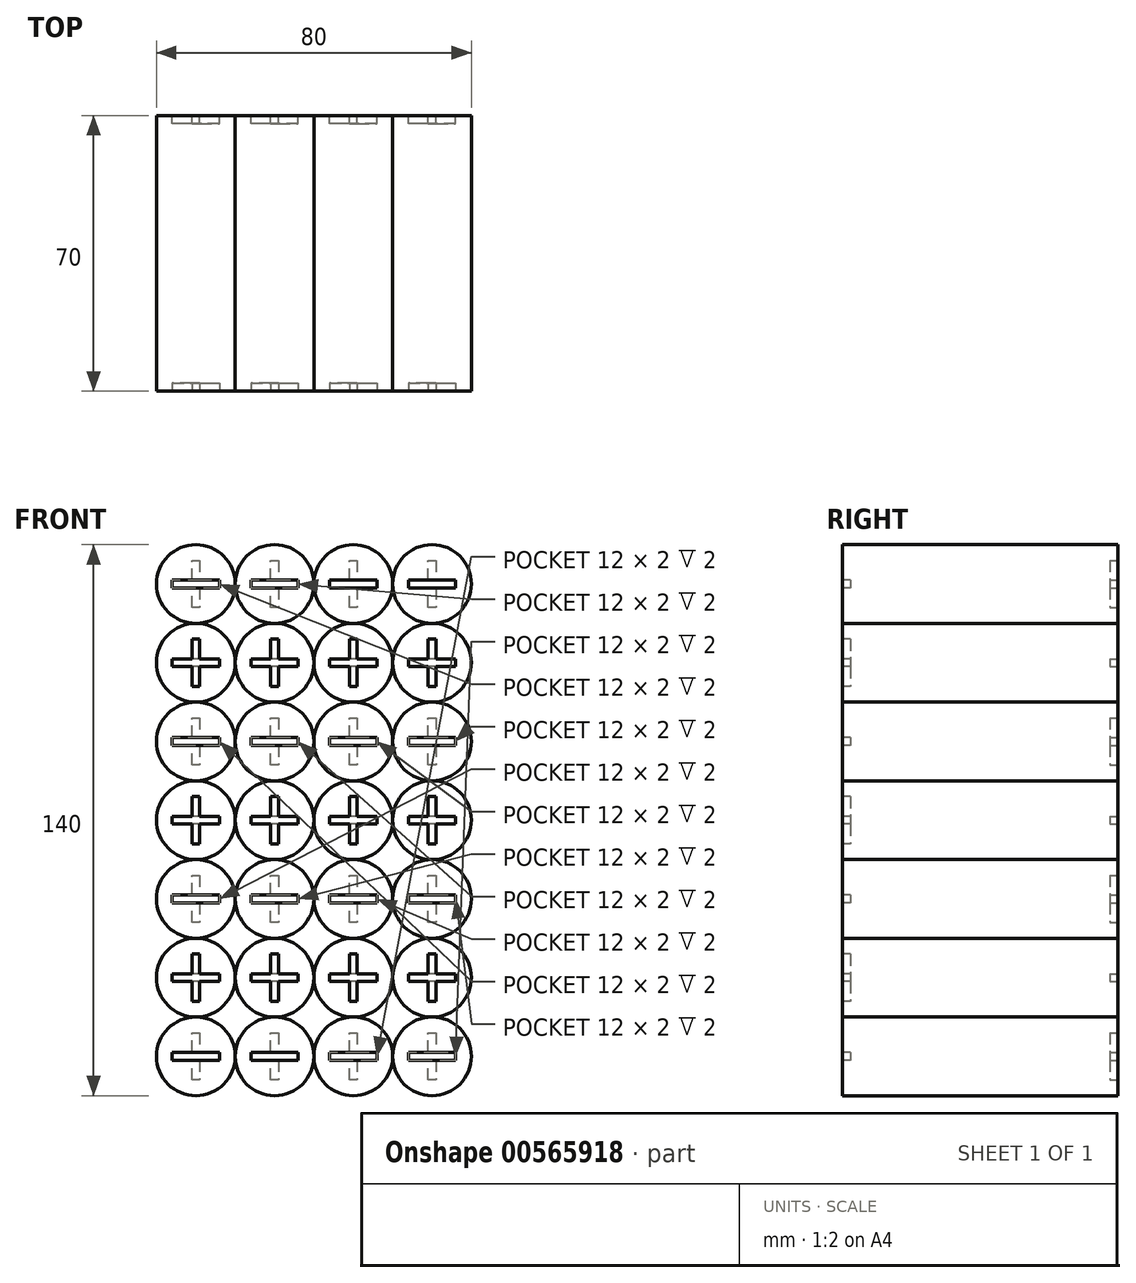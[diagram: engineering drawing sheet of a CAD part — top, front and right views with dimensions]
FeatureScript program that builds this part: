
annotation { "Feature Type Name" : "Feature", "Feature Type Description" : "" }
export const myFeature = defineFeature(function(context is Context, id is Id, definition is map)
    precondition{}
    {
        {
            var Q0;
            Q0=qCreatedBy(makeId("Front.planeOp"),FACE);
            var sketch = newSketch(context, id + "F0", { "sketchPlane" : qUnion([Q0])});
            skCircle(sketch, "E0", {"center": v(10, 10) * mm, "radius": 10 * mm});
            skCircle(sketch, "E1", {"center": v(30, 10) * mm, "radius": 10 * mm});
            skCircle(sketch, "E2", {"center": v(50, 10) * mm, "radius": 10 * mm});
            skCircle(sketch, "E3", {"center": v(70, 10) * mm, "radius": 10 * mm});
            skCircle(sketch, "E4", {"center": v(10, 30) * mm, "radius": 10 * mm});
            skCircle(sketch, "E5", {"center": v(30, 30) * mm, "radius": 10 * mm});
            skCircle(sketch, "E6", {"center": v(50, 30) * mm, "radius": 10 * mm});
            skCircle(sketch, "E7", {"center": v(70, 30) * mm, "radius": 10 * mm});
            skCircle(sketch, "E8", {"center": v(10, 50) * mm, "radius": 10 * mm});
            skCircle(sketch, "E9", {"center": v(30, 50) * mm, "radius": 10 * mm});
            skCircle(sketch, "E10", {"center": v(50, 50) * mm, "radius": 10 * mm});
            skCircle(sketch, "E11", {"center": v(70, 50) * mm, "radius": 10 * mm});
            skCircle(sketch, "E12", {"center": v(10, 70) * mm, "radius": 10 * mm});
            skCircle(sketch, "E13", {"center": v(30, 70) * mm, "radius": 10 * mm});
            skCircle(sketch, "E14", {"center": v(50, 70) * mm, "radius": 10 * mm});
            skCircle(sketch, "E15", {"center": v(70, 70) * mm, "radius": 10 * mm});
            skCircle(sketch, "E16", {"center": v(10, 90) * mm, "radius": 10 * mm});
            skCircle(sketch, "E17", {"center": v(30, 90) * mm, "radius": 10 * mm});
            skCircle(sketch, "E18", {"center": v(50, 90) * mm, "radius": 10 * mm});
            skCircle(sketch, "E19", {"center": v(70, 90) * mm, "radius": 10 * mm});
            skCircle(sketch, "E20", {"center": v(10, 110) * mm, "radius": 10 * mm});
            skCircle(sketch, "E21", {"center": v(30, 110) * mm, "radius": 10 * mm});
            skCircle(sketch, "E22", {"center": v(50, 110) * mm, "radius": 10 * mm});
            skCircle(sketch, "E23", {"center": v(70, 110) * mm, "radius": 10 * mm});
            skCircle(sketch, "E24", {"center": v(10, 130) * mm, "radius": 10 * mm});
            skCircle(sketch, "E25", {"center": v(30, 130) * mm, "radius": 10 * mm});
            skCircle(sketch, "E26", {"center": v(50, 130) * mm, "radius": 10 * mm});
            skCircle(sketch, "E27", {"center": v(70, 130) * mm, "radius": 10 * mm});
            skSolve(sketch);
        }
        {
            var Q0;
            Q0 = qSketchRegion(id + "F0", true);
            extrude(context, id + "F1", {"entities" : qUnion([Q0]), "depth" : 70 * mm, "offsetDistance" : 25 * mm});
        }
        {
            var Q0;
            Q0=makeQuery(id+"F1.opExtrude","CAP_FACE",FACE,{"disambiguationData":[OSD([sQuery(id+"F0.wireOp",EDGE,"E5")])],"isStart":true});
            var sketch = newSketch(context, id + "F2", { "sketchPlane" : qUnion([Q0])});
            skLineSegment(sketch, "E28", {"start": v(-71, 16) * mm, "end": v(-71, 11) * mm});
            skLineSegment(sketch, "E29", {"start": v(-71, 11) * mm, "end": v(-76, 11) * mm});
            skLineSegment(sketch, "E30", {"start": v(-76, 11) * mm, "end": v(-76, 9) * mm});
            skLineSegment(sketch, "E31", {"start": v(-76, 9) * mm, "end": v(-71, 9) * mm});
            skLineSegment(sketch, "E32", {"start": v(-71, 9) * mm, "end": v(-71, 4) * mm});
            skLineSegment(sketch, "E33", {"start": v(-71, 4) * mm, "end": v(-69, 4) * mm});
            skLineSegment(sketch, "E34", {"start": v(-69, 4) * mm, "end": v(-69, 9) * mm});
            skLineSegment(sketch, "E35", {"start": v(-69, 9) * mm, "end": v(-64, 9) * mm});
            skLineSegment(sketch, "E36", {"start": v(-64, 9) * mm, "end": v(-64, 11) * mm});
            skLineSegment(sketch, "E37", {"start": v(-64, 11) * mm, "end": v(-69, 11) * mm});
            skLineSegment(sketch, "E38", {"start": v(-69, 11) * mm, "end": v(-69, 16) * mm});
            skLineSegment(sketch, "E39", {"start": v(-69, 16) * mm, "end": v(-71, 16) * mm});
            skLineSegment(sketch, "E40", {"start": v(-11, 16) * mm, "end": v(-11, 11) * mm});
            skLineSegment(sketch, "E41", {"start": v(-11, 11) * mm, "end": v(-16, 11) * mm});
            skLineSegment(sketch, "E42", {"start": v(-16, 11) * mm, "end": v(-16, 9) * mm});
            skLineSegment(sketch, "E43", {"start": v(-16, 9) * mm, "end": v(-11, 9) * mm});
            skLineSegment(sketch, "E44", {"start": v(-11, 9) * mm, "end": v(-11, 4) * mm});
            skLineSegment(sketch, "E45", {"start": v(-11, 4) * mm, "end": v(-9, 4) * mm});
            skLineSegment(sketch, "E46", {"start": v(-9, 4) * mm, "end": v(-9, 9) * mm});
            skLineSegment(sketch, "E47", {"start": v(-9, 9) * mm, "end": v(-4, 9) * mm});
            skLineSegment(sketch, "E48", {"start": v(-4, 9) * mm, "end": v(-4, 11) * mm});
            skLineSegment(sketch, "E49", {"start": v(-4, 11) * mm, "end": v(-9, 11) * mm});
            skLineSegment(sketch, "E50", {"start": v(-9, 11) * mm, "end": v(-9, 16) * mm});
            skLineSegment(sketch, "E51", {"start": v(-9, 16) * mm, "end": v(-11, 16) * mm});
            skLineSegment(sketch, "E52", {"start": v(-31, 16) * mm, "end": v(-31, 11) * mm});
            skLineSegment(sketch, "E53", {"start": v(-31, 11) * mm, "end": v(-36, 11) * mm});
            skLineSegment(sketch, "E54", {"start": v(-36, 11) * mm, "end": v(-36, 9) * mm});
            skLineSegment(sketch, "E55", {"start": v(-36, 9) * mm, "end": v(-31, 9) * mm});
            skLineSegment(sketch, "E56", {"start": v(-31, 9) * mm, "end": v(-31, 4) * mm});
            skLineSegment(sketch, "E57", {"start": v(-31, 4) * mm, "end": v(-29, 4) * mm});
            skLineSegment(sketch, "E58", {"start": v(-29, 4) * mm, "end": v(-29, 9) * mm});
            skLineSegment(sketch, "E59", {"start": v(-29, 9) * mm, "end": v(-24, 9) * mm});
            skLineSegment(sketch, "E60", {"start": v(-24, 9) * mm, "end": v(-24, 11) * mm});
            skLineSegment(sketch, "E61", {"start": v(-24, 11) * mm, "end": v(-29, 11) * mm});
            skLineSegment(sketch, "E62", {"start": v(-29, 11) * mm, "end": v(-29, 16) * mm});
            skLineSegment(sketch, "E63", {"start": v(-29, 16) * mm, "end": v(-31, 16) * mm});
            skLineSegment(sketch, "E64", {"start": v(-51, 16) * mm, "end": v(-51, 11) * mm});
            skLineSegment(sketch, "E65", {"start": v(-51, 11) * mm, "end": v(-56, 11) * mm});
            skLineSegment(sketch, "E66", {"start": v(-56, 11) * mm, "end": v(-56, 9) * mm});
            skLineSegment(sketch, "E67", {"start": v(-56, 9) * mm, "end": v(-51, 9) * mm});
            skLineSegment(sketch, "E68", {"start": v(-51, 9) * mm, "end": v(-51, 4) * mm});
            skLineSegment(sketch, "E69", {"start": v(-51, 4) * mm, "end": v(-49, 4) * mm});
            skLineSegment(sketch, "E70", {"start": v(-49, 4) * mm, "end": v(-49, 9) * mm});
            skLineSegment(sketch, "E71", {"start": v(-49, 9) * mm, "end": v(-44, 9) * mm});
            skLineSegment(sketch, "E72", {"start": v(-44, 9) * mm, "end": v(-44, 11) * mm});
            skLineSegment(sketch, "E73", {"start": v(-44, 11) * mm, "end": v(-49, 11) * mm});
            skLineSegment(sketch, "E74", {"start": v(-49, 11) * mm, "end": v(-49, 16) * mm});
            skLineSegment(sketch, "E75", {"start": v(-49, 16) * mm, "end": v(-51, 16) * mm});
            skLineSegment(sketch, "E76", {"start": v(-71, 56) * mm, "end": v(-71, 51) * mm});
            skLineSegment(sketch, "E77", {"start": v(-71, 51) * mm, "end": v(-76, 51) * mm});
            skLineSegment(sketch, "E78", {"start": v(-76, 51) * mm, "end": v(-76, 49) * mm});
            skLineSegment(sketch, "E79", {"start": v(-76, 49) * mm, "end": v(-71, 49) * mm});
            skLineSegment(sketch, "E80", {"start": v(-71, 49) * mm, "end": v(-71, 44) * mm});
            skLineSegment(sketch, "E81", {"start": v(-71, 44) * mm, "end": v(-69, 44) * mm});
            skLineSegment(sketch, "E82", {"start": v(-69, 44) * mm, "end": v(-69, 49) * mm});
            skLineSegment(sketch, "E83", {"start": v(-69, 49) * mm, "end": v(-64, 49) * mm});
            skLineSegment(sketch, "E84", {"start": v(-64, 49) * mm, "end": v(-64, 51) * mm});
            skLineSegment(sketch, "E85", {"start": v(-64, 51) * mm, "end": v(-69, 51) * mm});
            skLineSegment(sketch, "E86", {"start": v(-69, 51) * mm, "end": v(-69, 56) * mm});
            skLineSegment(sketch, "E87", {"start": v(-69, 56) * mm, "end": v(-71, 56) * mm});
            skLineSegment(sketch, "E88", {"start": v(-11, 56) * mm, "end": v(-11, 51) * mm});
            skLineSegment(sketch, "E89", {"start": v(-11, 51) * mm, "end": v(-16, 51) * mm});
            skLineSegment(sketch, "E90", {"start": v(-16, 51) * mm, "end": v(-16, 49) * mm});
            skLineSegment(sketch, "E91", {"start": v(-16, 49) * mm, "end": v(-11, 49) * mm});
            skLineSegment(sketch, "E92", {"start": v(-11, 49) * mm, "end": v(-11, 44) * mm});
            skLineSegment(sketch, "E93", {"start": v(-11, 44) * mm, "end": v(-9, 44) * mm});
            skLineSegment(sketch, "E94", {"start": v(-9, 44) * mm, "end": v(-9, 49) * mm});
            skLineSegment(sketch, "E95", {"start": v(-9, 49) * mm, "end": v(-4, 49) * mm});
            skLineSegment(sketch, "E96", {"start": v(-4, 49) * mm, "end": v(-4, 51) * mm});
            skLineSegment(sketch, "E97", {"start": v(-4, 51) * mm, "end": v(-9, 51) * mm});
            skLineSegment(sketch, "E98", {"start": v(-9, 51) * mm, "end": v(-9, 56) * mm});
            skLineSegment(sketch, "E99", {"start": v(-9, 56) * mm, "end": v(-11, 56) * mm});
            skLineSegment(sketch, "E100", {"start": v(-31, 56) * mm, "end": v(-31, 51) * mm});
            skLineSegment(sketch, "E101", {"start": v(-31, 51) * mm, "end": v(-36, 51) * mm});
            skLineSegment(sketch, "E102", {"start": v(-36, 51) * mm, "end": v(-36, 49) * mm});
            skLineSegment(sketch, "E103", {"start": v(-36, 49) * mm, "end": v(-31, 49) * mm});
            skLineSegment(sketch, "E104", {"start": v(-31, 49) * mm, "end": v(-31, 44) * mm});
            skLineSegment(sketch, "E105", {"start": v(-31, 44) * mm, "end": v(-29, 44) * mm});
            skLineSegment(sketch, "E106", {"start": v(-29, 44) * mm, "end": v(-29, 49) * mm});
            skLineSegment(sketch, "E107", {"start": v(-29, 49) * mm, "end": v(-24, 49) * mm});
            skLineSegment(sketch, "E108", {"start": v(-24, 49) * mm, "end": v(-24, 51) * mm});
            skLineSegment(sketch, "E109", {"start": v(-24, 51) * mm, "end": v(-29, 51) * mm});
            skLineSegment(sketch, "E110", {"start": v(-29, 51) * mm, "end": v(-29, 56) * mm});
            skLineSegment(sketch, "E111", {"start": v(-29, 56) * mm, "end": v(-31, 56) * mm});
            skLineSegment(sketch, "E112", {"start": v(-51, 56) * mm, "end": v(-51, 51) * mm});
            skLineSegment(sketch, "E113", {"start": v(-51, 51) * mm, "end": v(-56, 51) * mm});
            skLineSegment(sketch, "E114", {"start": v(-56, 51) * mm, "end": v(-56, 49) * mm});
            skLineSegment(sketch, "E115", {"start": v(-56, 49) * mm, "end": v(-51, 49) * mm});
            skLineSegment(sketch, "E116", {"start": v(-51, 49) * mm, "end": v(-51, 44) * mm});
            skLineSegment(sketch, "E117", {"start": v(-51, 44) * mm, "end": v(-49, 44) * mm});
            skLineSegment(sketch, "E118", {"start": v(-49, 44) * mm, "end": v(-49, 49) * mm});
            skLineSegment(sketch, "E119", {"start": v(-49, 49) * mm, "end": v(-44, 49) * mm});
            skLineSegment(sketch, "E120", {"start": v(-44, 49) * mm, "end": v(-44, 51) * mm});
            skLineSegment(sketch, "E121", {"start": v(-44, 51) * mm, "end": v(-49, 51) * mm});
            skLineSegment(sketch, "E122", {"start": v(-49, 51) * mm, "end": v(-49, 56) * mm});
            skLineSegment(sketch, "E123", {"start": v(-49, 56) * mm, "end": v(-51, 56) * mm});
            skLineSegment(sketch, "E124", {"start": v(-71, 96) * mm, "end": v(-71, 91) * mm});
            skLineSegment(sketch, "E125", {"start": v(-71, 91) * mm, "end": v(-76, 91) * mm});
            skLineSegment(sketch, "E126", {"start": v(-76, 91) * mm, "end": v(-76, 89) * mm});
            skLineSegment(sketch, "E127", {"start": v(-76, 89) * mm, "end": v(-71, 89) * mm});
            skLineSegment(sketch, "E128", {"start": v(-71, 89) * mm, "end": v(-71, 84) * mm});
            skLineSegment(sketch, "E129", {"start": v(-71, 84) * mm, "end": v(-69, 84) * mm});
            skLineSegment(sketch, "E130", {"start": v(-69, 84) * mm, "end": v(-69, 89) * mm});
            skLineSegment(sketch, "E131", {"start": v(-69, 89) * mm, "end": v(-64, 89) * mm});
            skLineSegment(sketch, "E132", {"start": v(-64, 89) * mm, "end": v(-64, 91) * mm});
            skLineSegment(sketch, "E133", {"start": v(-64, 91) * mm, "end": v(-69, 91) * mm});
            skLineSegment(sketch, "E134", {"start": v(-69, 91) * mm, "end": v(-69, 96) * mm});
            skLineSegment(sketch, "E135", {"start": v(-69, 96) * mm, "end": v(-71, 96) * mm});
            skLineSegment(sketch, "E136", {"start": v(-11, 96) * mm, "end": v(-11, 91) * mm});
            skLineSegment(sketch, "E137", {"start": v(-11, 91) * mm, "end": v(-16, 91) * mm});
            skLineSegment(sketch, "E138", {"start": v(-16, 91) * mm, "end": v(-16, 89) * mm});
            skLineSegment(sketch, "E139", {"start": v(-16, 89) * mm, "end": v(-11, 89) * mm});
            skLineSegment(sketch, "E140", {"start": v(-11, 89) * mm, "end": v(-11, 84) * mm});
            skLineSegment(sketch, "E141", {"start": v(-11, 84) * mm, "end": v(-9, 84) * mm});
            skLineSegment(sketch, "E142", {"start": v(-9, 84) * mm, "end": v(-9, 89) * mm});
            skLineSegment(sketch, "E143", {"start": v(-9, 89) * mm, "end": v(-4, 89) * mm});
            skLineSegment(sketch, "E144", {"start": v(-4, 89) * mm, "end": v(-4, 91) * mm});
            skLineSegment(sketch, "E145", {"start": v(-4, 91) * mm, "end": v(-9, 91) * mm});
            skLineSegment(sketch, "E146", {"start": v(-9, 91) * mm, "end": v(-9, 96) * mm});
            skLineSegment(sketch, "E147", {"start": v(-9, 96) * mm, "end": v(-11, 96) * mm});
            skLineSegment(sketch, "E148", {"start": v(-31, 96) * mm, "end": v(-31, 91) * mm});
            skLineSegment(sketch, "E149", {"start": v(-31, 91) * mm, "end": v(-36, 91) * mm});
            skLineSegment(sketch, "E150", {"start": v(-36, 91) * mm, "end": v(-36, 89) * mm});
            skLineSegment(sketch, "E151", {"start": v(-36, 89) * mm, "end": v(-31, 89) * mm});
            skLineSegment(sketch, "E152", {"start": v(-31, 89) * mm, "end": v(-31, 84) * mm});
            skLineSegment(sketch, "E153", {"start": v(-31, 84) * mm, "end": v(-29, 84) * mm});
            skLineSegment(sketch, "E154", {"start": v(-29, 84) * mm, "end": v(-29, 89) * mm});
            skLineSegment(sketch, "E155", {"start": v(-29, 89) * mm, "end": v(-24, 89) * mm});
            skLineSegment(sketch, "E156", {"start": v(-24, 89) * mm, "end": v(-24, 91) * mm});
            skLineSegment(sketch, "E157", {"start": v(-24, 91) * mm, "end": v(-29, 91) * mm});
            skLineSegment(sketch, "E158", {"start": v(-29, 91) * mm, "end": v(-29, 96) * mm});
            skLineSegment(sketch, "E159", {"start": v(-29, 96) * mm, "end": v(-31, 96) * mm});
            skLineSegment(sketch, "E160", {"start": v(-51, 96) * mm, "end": v(-51, 91) * mm});
            skLineSegment(sketch, "E161", {"start": v(-51, 91) * mm, "end": v(-56, 91) * mm});
            skLineSegment(sketch, "E162", {"start": v(-56, 91) * mm, "end": v(-56, 89) * mm});
            skLineSegment(sketch, "E163", {"start": v(-56, 89) * mm, "end": v(-51, 89) * mm});
            skLineSegment(sketch, "E164", {"start": v(-51, 89) * mm, "end": v(-51, 84) * mm});
            skLineSegment(sketch, "E165", {"start": v(-51, 84) * mm, "end": v(-49, 84) * mm});
            skLineSegment(sketch, "E166", {"start": v(-49, 84) * mm, "end": v(-49, 89) * mm});
            skLineSegment(sketch, "E167", {"start": v(-49, 89) * mm, "end": v(-44, 89) * mm});
            skLineSegment(sketch, "E168", {"start": v(-44, 89) * mm, "end": v(-44, 91) * mm});
            skLineSegment(sketch, "E169", {"start": v(-44, 91) * mm, "end": v(-49, 91) * mm});
            skLineSegment(sketch, "E170", {"start": v(-49, 91) * mm, "end": v(-49, 96) * mm});
            skLineSegment(sketch, "E171", {"start": v(-49, 96) * mm, "end": v(-51, 96) * mm});
            skLineSegment(sketch, "E172", {"start": v(-71, 136) * mm, "end": v(-71, 131) * mm});
            skLineSegment(sketch, "E173", {"start": v(-71, 131) * mm, "end": v(-76, 131) * mm});
            skLineSegment(sketch, "E174", {"start": v(-76, 131) * mm, "end": v(-76, 129) * mm});
            skLineSegment(sketch, "E175", {"start": v(-76, 129) * mm, "end": v(-71, 129) * mm});
            skLineSegment(sketch, "E176", {"start": v(-71, 129) * mm, "end": v(-71, 124) * mm});
            skLineSegment(sketch, "E177", {"start": v(-71, 124) * mm, "end": v(-69, 124) * mm});
            skLineSegment(sketch, "E178", {"start": v(-69, 124) * mm, "end": v(-69, 129) * mm});
            skLineSegment(sketch, "E179", {"start": v(-69, 129) * mm, "end": v(-64, 129) * mm});
            skLineSegment(sketch, "E180", {"start": v(-64, 129) * mm, "end": v(-64, 131) * mm});
            skLineSegment(sketch, "E181", {"start": v(-64, 131) * mm, "end": v(-69, 131) * mm});
            skLineSegment(sketch, "E182", {"start": v(-69, 131) * mm, "end": v(-69, 136) * mm});
            skLineSegment(sketch, "E183", {"start": v(-69, 136) * mm, "end": v(-71, 136) * mm});
            skLineSegment(sketch, "E184", {"start": v(-11, 136) * mm, "end": v(-11, 131) * mm});
            skLineSegment(sketch, "E185", {"start": v(-11, 131) * mm, "end": v(-16, 131) * mm});
            skLineSegment(sketch, "E186", {"start": v(-16, 131) * mm, "end": v(-16, 129) * mm});
            skLineSegment(sketch, "E187", {"start": v(-16, 129) * mm, "end": v(-11, 129) * mm});
            skLineSegment(sketch, "E188", {"start": v(-11, 129) * mm, "end": v(-11, 124) * mm});
            skLineSegment(sketch, "E189", {"start": v(-11, 124) * mm, "end": v(-9, 124) * mm});
            skLineSegment(sketch, "E190", {"start": v(-9, 124) * mm, "end": v(-9, 129) * mm});
            skLineSegment(sketch, "E191", {"start": v(-9, 129) * mm, "end": v(-4, 129) * mm});
            skLineSegment(sketch, "E192", {"start": v(-4, 129) * mm, "end": v(-4, 131) * mm});
            skLineSegment(sketch, "E193", {"start": v(-4, 131) * mm, "end": v(-9, 131) * mm});
            skLineSegment(sketch, "E194", {"start": v(-9, 131) * mm, "end": v(-9, 136) * mm});
            skLineSegment(sketch, "E195", {"start": v(-9, 136) * mm, "end": v(-11, 136) * mm});
            skLineSegment(sketch, "E196", {"start": v(-31, 136) * mm, "end": v(-31, 131) * mm});
            skLineSegment(sketch, "E197", {"start": v(-31, 131) * mm, "end": v(-36, 131) * mm});
            skLineSegment(sketch, "E198", {"start": v(-36, 131) * mm, "end": v(-36, 129) * mm});
            skLineSegment(sketch, "E199", {"start": v(-36, 129) * mm, "end": v(-31, 129) * mm});
            skLineSegment(sketch, "E200", {"start": v(-31, 129) * mm, "end": v(-31, 124) * mm});
            skLineSegment(sketch, "E201", {"start": v(-31, 124) * mm, "end": v(-29, 124) * mm});
            skLineSegment(sketch, "E202", {"start": v(-29, 124) * mm, "end": v(-29, 129) * mm});
            skLineSegment(sketch, "E203", {"start": v(-29, 129) * mm, "end": v(-24, 129) * mm});
            skLineSegment(sketch, "E204", {"start": v(-24, 129) * mm, "end": v(-24, 131) * mm});
            skLineSegment(sketch, "E205", {"start": v(-24, 131) * mm, "end": v(-29, 131) * mm});
            skLineSegment(sketch, "E206", {"start": v(-29, 131) * mm, "end": v(-29, 136) * mm});
            skLineSegment(sketch, "E207", {"start": v(-29, 136) * mm, "end": v(-31, 136) * mm});
            skLineSegment(sketch, "E208", {"start": v(-51, 136) * mm, "end": v(-51, 131) * mm});
            skLineSegment(sketch, "E209", {"start": v(-51, 131) * mm, "end": v(-56, 131) * mm});
            skLineSegment(sketch, "E210", {"start": v(-56, 131) * mm, "end": v(-56, 129) * mm});
            skLineSegment(sketch, "E211", {"start": v(-56, 129) * mm, "end": v(-51, 129) * mm});
            skLineSegment(sketch, "E212", {"start": v(-51, 129) * mm, "end": v(-51, 124) * mm});
            skLineSegment(sketch, "E213", {"start": v(-51, 124) * mm, "end": v(-49, 124) * mm});
            skLineSegment(sketch, "E214", {"start": v(-49, 124) * mm, "end": v(-49, 129) * mm});
            skLineSegment(sketch, "E215", {"start": v(-49, 129) * mm, "end": v(-44, 129) * mm});
            skLineSegment(sketch, "E216", {"start": v(-44, 129) * mm, "end": v(-44, 131) * mm});
            skLineSegment(sketch, "E217", {"start": v(-44, 131) * mm, "end": v(-49, 131) * mm});
            skLineSegment(sketch, "E218", {"start": v(-49, 131) * mm, "end": v(-49, 136) * mm});
            skLineSegment(sketch, "E219", {"start": v(-49, 136) * mm, "end": v(-51, 136) * mm});
            skLineSegment(sketch, "E220.bottom", {"start": v(-76, 31) * mm, "end": v(-64, 31) * mm});
            skLineSegment(sketch, "E220.top", {"start": v(-76, 29) * mm, "end": v(-64, 29) * mm});
            skLineSegment(sketch, "E220.left", {"start": v(-76, 31) * mm, "end": v(-76, 29) * mm});
            skLineSegment(sketch, "E220.right", {"start": v(-64, 31) * mm, "end": v(-64, 29) * mm});
            skLineSegment(sketch, "E221.bottom", {"start": v(-56, 31) * mm, "end": v(-44, 31) * mm});
            skLineSegment(sketch, "E221.top", {"start": v(-56, 29) * mm, "end": v(-44, 29) * mm});
            skLineSegment(sketch, "E221.left", {"start": v(-56, 31) * mm, "end": v(-56, 29) * mm});
            skLineSegment(sketch, "E221.right", {"start": v(-44, 31) * mm, "end": v(-44, 29) * mm});
            skLineSegment(sketch, "E222.bottom", {"start": v(-36, 31) * mm, "end": v(-24, 31) * mm});
            skLineSegment(sketch, "E222.top", {"start": v(-36, 29) * mm, "end": v(-24, 29) * mm});
            skLineSegment(sketch, "E222.left", {"start": v(-36, 31) * mm, "end": v(-36, 29) * mm});
            skLineSegment(sketch, "E222.right", {"start": v(-24, 31) * mm, "end": v(-24, 29) * mm});
            skLineSegment(sketch, "E223.bottom", {"start": v(-16, 31) * mm, "end": v(-4, 31) * mm});
            skLineSegment(sketch, "E223.top", {"start": v(-16, 29) * mm, "end": v(-4, 29) * mm});
            skLineSegment(sketch, "E223.left", {"start": v(-16, 31) * mm, "end": v(-16, 29) * mm});
            skLineSegment(sketch, "E223.right", {"start": v(-4, 31) * mm, "end": v(-4, 29) * mm});
            skLineSegment(sketch, "E224.bottom", {"start": v(-76, 71) * mm, "end": v(-64, 71) * mm});
            skLineSegment(sketch, "E224.top", {"start": v(-76, 69) * mm, "end": v(-64, 69) * mm});
            skLineSegment(sketch, "E224.left", {"start": v(-76, 71) * mm, "end": v(-76, 69) * mm});
            skLineSegment(sketch, "E224.right", {"start": v(-64, 71) * mm, "end": v(-64, 69) * mm});
            skLineSegment(sketch, "E225.bottom", {"start": v(-56, 71) * mm, "end": v(-44, 71) * mm});
            skLineSegment(sketch, "E225.top", {"start": v(-56, 69) * mm, "end": v(-44, 69) * mm});
            skLineSegment(sketch, "E225.left", {"start": v(-56, 71) * mm, "end": v(-56, 69) * mm});
            skLineSegment(sketch, "E225.right", {"start": v(-44, 71) * mm, "end": v(-44, 69) * mm});
            skLineSegment(sketch, "E226.bottom", {"start": v(-36, 71) * mm, "end": v(-24, 71) * mm});
            skLineSegment(sketch, "E226.top", {"start": v(-36, 69) * mm, "end": v(-24, 69) * mm});
            skLineSegment(sketch, "E226.left", {"start": v(-36, 71) * mm, "end": v(-36, 69) * mm});
            skLineSegment(sketch, "E226.right", {"start": v(-24, 71) * mm, "end": v(-24, 69) * mm});
            skLineSegment(sketch, "E227.bottom", {"start": v(-16, 71) * mm, "end": v(-4, 71) * mm});
            skLineSegment(sketch, "E227.top", {"start": v(-16, 69) * mm, "end": v(-4, 69) * mm});
            skLineSegment(sketch, "E227.left", {"start": v(-16, 71) * mm, "end": v(-16, 69) * mm});
            skLineSegment(sketch, "E227.right", {"start": v(-4, 71) * mm, "end": v(-4, 69) * mm});
            skLineSegment(sketch, "E228.bottom", {"start": v(-76, 111) * mm, "end": v(-64, 111) * mm});
            skLineSegment(sketch, "E228.top", {"start": v(-76, 109) * mm, "end": v(-64, 109) * mm});
            skLineSegment(sketch, "E228.left", {"start": v(-76, 111) * mm, "end": v(-76, 109) * mm});
            skLineSegment(sketch, "E228.right", {"start": v(-64, 111) * mm, "end": v(-64, 109) * mm});
            skLineSegment(sketch, "E229.bottom", {"start": v(-56, 111) * mm, "end": v(-44, 111) * mm});
            skLineSegment(sketch, "E229.top", {"start": v(-56, 109) * mm, "end": v(-44, 109) * mm});
            skLineSegment(sketch, "E229.left", {"start": v(-56, 111) * mm, "end": v(-56, 109) * mm});
            skLineSegment(sketch, "E229.right", {"start": v(-44, 111) * mm, "end": v(-44, 109) * mm});
            skLineSegment(sketch, "E230.bottom", {"start": v(-36, 111) * mm, "end": v(-24, 111) * mm});
            skLineSegment(sketch, "E230.top", {"start": v(-36, 109) * mm, "end": v(-24, 109) * mm});
            skLineSegment(sketch, "E230.left", {"start": v(-36, 111) * mm, "end": v(-36, 109) * mm});
            skLineSegment(sketch, "E230.right", {"start": v(-24, 111) * mm, "end": v(-24, 109) * mm});
            skLineSegment(sketch, "E231.bottom", {"start": v(-16, 111) * mm, "end": v(-4, 111) * mm});
            skLineSegment(sketch, "E231.top", {"start": v(-16, 109) * mm, "end": v(-4, 109) * mm});
            skLineSegment(sketch, "E231.left", {"start": v(-16, 111) * mm, "end": v(-16, 109) * mm});
            skLineSegment(sketch, "E231.right", {"start": v(-4, 111) * mm, "end": v(-4, 109) * mm});
            skSolve(sketch);
        }
        {
            var Q0;
            Q0 = qSketchRegion(id + "F2", true);
            extrude(context, id + "F3", {"entities" : qUnion([Q0]), "operationType" : NewBodyOperationType.REMOVE, "oppositeDirection" : true, "depth" : 2 * mm, "offsetDistance" : 25 * mm});
        }
        {
            var Q0;
            Q0=makeQuery(id+"F1.opExtrude","CAP_FACE",FACE,{"disambiguationData":[OSD([sQuery(id+"F0.wireOp",EDGE,"E20")])],"isStart":false});
            var sketch = newSketch(context, id + "F4", { "sketchPlane" : qUnion([Q0])});
            skLineSegment(sketch, "E232", {"start": v(9, 36) * mm, "end": v(9, 31) * mm});
            skLineSegment(sketch, "E233", {"start": v(9, 31) * mm, "end": v(4, 31) * mm});
            skLineSegment(sketch, "E234", {"start": v(4, 31) * mm, "end": v(4, 29) * mm});
            skLineSegment(sketch, "E235", {"start": v(4, 29) * mm, "end": v(9, 29) * mm});
            skLineSegment(sketch, "E236", {"start": v(9, 29) * mm, "end": v(9, 24) * mm});
            skLineSegment(sketch, "E237", {"start": v(9, 24) * mm, "end": v(11, 24) * mm});
            skLineSegment(sketch, "E238", {"start": v(11, 24) * mm, "end": v(11, 29) * mm});
            skLineSegment(sketch, "E239", {"start": v(11, 29) * mm, "end": v(16, 29) * mm});
            skLineSegment(sketch, "E240", {"start": v(16, 29) * mm, "end": v(16, 31) * mm});
            skLineSegment(sketch, "E241", {"start": v(16, 31) * mm, "end": v(11, 31) * mm});
            skLineSegment(sketch, "E242", {"start": v(11, 31) * mm, "end": v(11, 36) * mm});
            skLineSegment(sketch, "E243", {"start": v(11, 36) * mm, "end": v(9, 36) * mm});
            skLineSegment(sketch, "E244", {"start": v(29, 36) * mm, "end": v(29, 31) * mm});
            skLineSegment(sketch, "E245", {"start": v(29, 31) * mm, "end": v(24, 31) * mm});
            skLineSegment(sketch, "E246", {"start": v(24, 31) * mm, "end": v(24, 29) * mm});
            skLineSegment(sketch, "E247", {"start": v(24, 29) * mm, "end": v(29, 29) * mm});
            skLineSegment(sketch, "E248", {"start": v(29, 29) * mm, "end": v(29, 24) * mm});
            skLineSegment(sketch, "E249", {"start": v(29, 24) * mm, "end": v(31, 24) * mm});
            skLineSegment(sketch, "E250", {"start": v(31, 24) * mm, "end": v(31, 29) * mm});
            skLineSegment(sketch, "E251", {"start": v(31, 29) * mm, "end": v(36, 29) * mm});
            skLineSegment(sketch, "E252", {"start": v(36, 29) * mm, "end": v(36, 31) * mm});
            skLineSegment(sketch, "E253", {"start": v(36, 31) * mm, "end": v(31, 31) * mm});
            skLineSegment(sketch, "E254", {"start": v(31, 31) * mm, "end": v(31, 36) * mm});
            skLineSegment(sketch, "E255", {"start": v(31, 36) * mm, "end": v(29, 36) * mm});
            skLineSegment(sketch, "E256", {"start": v(69, 36) * mm, "end": v(69, 31) * mm});
            skLineSegment(sketch, "E257", {"start": v(69, 31) * mm, "end": v(64, 31) * mm});
            skLineSegment(sketch, "E258", {"start": v(64, 31) * mm, "end": v(64, 29) * mm});
            skLineSegment(sketch, "E259", {"start": v(64, 29) * mm, "end": v(69, 29) * mm});
            skLineSegment(sketch, "E260", {"start": v(69, 29) * mm, "end": v(69, 24) * mm});
            skLineSegment(sketch, "E261", {"start": v(69, 24) * mm, "end": v(71, 24) * mm});
            skLineSegment(sketch, "E262", {"start": v(71, 24) * mm, "end": v(71, 29) * mm});
            skLineSegment(sketch, "E263", {"start": v(71, 29) * mm, "end": v(76, 29) * mm});
            skLineSegment(sketch, "E264", {"start": v(76, 29) * mm, "end": v(76, 31) * mm});
            skLineSegment(sketch, "E265", {"start": v(76, 31) * mm, "end": v(71, 31) * mm});
            skLineSegment(sketch, "E266", {"start": v(71, 31) * mm, "end": v(71, 36) * mm});
            skLineSegment(sketch, "E267", {"start": v(71, 36) * mm, "end": v(69, 36) * mm});
            skLineSegment(sketch, "E268", {"start": v(49, 36) * mm, "end": v(49, 31) * mm});
            skLineSegment(sketch, "E269", {"start": v(49, 31) * mm, "end": v(44, 31) * mm});
            skLineSegment(sketch, "E270", {"start": v(44, 31) * mm, "end": v(44, 29) * mm});
            skLineSegment(sketch, "E271", {"start": v(44, 29) * mm, "end": v(49, 29) * mm});
            skLineSegment(sketch, "E272", {"start": v(49, 29) * mm, "end": v(49, 24) * mm});
            skLineSegment(sketch, "E273", {"start": v(49, 24) * mm, "end": v(51, 24) * mm});
            skLineSegment(sketch, "E274", {"start": v(51, 24) * mm, "end": v(51, 29) * mm});
            skLineSegment(sketch, "E275", {"start": v(51, 29) * mm, "end": v(56, 29) * mm});
            skLineSegment(sketch, "E276", {"start": v(56, 29) * mm, "end": v(56, 31) * mm});
            skLineSegment(sketch, "E277", {"start": v(56, 31) * mm, "end": v(51, 31) * mm});
            skLineSegment(sketch, "E278", {"start": v(51, 31) * mm, "end": v(51, 36) * mm});
            skLineSegment(sketch, "E279", {"start": v(51, 36) * mm, "end": v(49, 36) * mm});
            skLineSegment(sketch, "E280", {"start": v(9, 76) * mm, "end": v(9, 71) * mm});
            skLineSegment(sketch, "E281", {"start": v(9, 71) * mm, "end": v(4, 71) * mm});
            skLineSegment(sketch, "E282", {"start": v(4, 71) * mm, "end": v(4, 69) * mm});
            skLineSegment(sketch, "E283", {"start": v(4, 69) * mm, "end": v(9, 69) * mm});
            skLineSegment(sketch, "E284", {"start": v(9, 69) * mm, "end": v(9, 64) * mm});
            skLineSegment(sketch, "E285", {"start": v(9, 64) * mm, "end": v(11, 64) * mm});
            skLineSegment(sketch, "E286", {"start": v(11, 64) * mm, "end": v(11, 69) * mm});
            skLineSegment(sketch, "E287", {"start": v(11, 69) * mm, "end": v(16, 69) * mm});
            skLineSegment(sketch, "E288", {"start": v(16, 69) * mm, "end": v(16, 71) * mm});
            skLineSegment(sketch, "E289", {"start": v(16, 71) * mm, "end": v(11, 71) * mm});
            skLineSegment(sketch, "E290", {"start": v(11, 71) * mm, "end": v(11, 76) * mm});
            skLineSegment(sketch, "E291", {"start": v(11, 76) * mm, "end": v(9, 76) * mm});
            skLineSegment(sketch, "E292", {"start": v(29, 76) * mm, "end": v(29, 71) * mm});
            skLineSegment(sketch, "E293", {"start": v(29, 71) * mm, "end": v(24, 71) * mm});
            skLineSegment(sketch, "E294", {"start": v(24, 71) * mm, "end": v(24, 69) * mm});
            skLineSegment(sketch, "E295", {"start": v(24, 69) * mm, "end": v(29, 69) * mm});
            skLineSegment(sketch, "E296", {"start": v(29, 69) * mm, "end": v(29, 64) * mm});
            skLineSegment(sketch, "E297", {"start": v(29, 64) * mm, "end": v(31, 64) * mm});
            skLineSegment(sketch, "E298", {"start": v(31, 64) * mm, "end": v(31, 69) * mm});
            skLineSegment(sketch, "E299", {"start": v(31, 69) * mm, "end": v(36, 69) * mm});
            skLineSegment(sketch, "E300", {"start": v(36, 69) * mm, "end": v(36, 71) * mm});
            skLineSegment(sketch, "E301", {"start": v(36, 71) * mm, "end": v(31, 71) * mm});
            skLineSegment(sketch, "E302", {"start": v(31, 71) * mm, "end": v(31, 76) * mm});
            skLineSegment(sketch, "E303", {"start": v(31, 76) * mm, "end": v(29, 76) * mm});
            skLineSegment(sketch, "E304", {"start": v(69, 76) * mm, "end": v(69, 71) * mm});
            skLineSegment(sketch, "E305", {"start": v(69, 71) * mm, "end": v(64, 71) * mm});
            skLineSegment(sketch, "E306", {"start": v(64, 71) * mm, "end": v(64, 69) * mm});
            skLineSegment(sketch, "E307", {"start": v(64, 69) * mm, "end": v(69, 69) * mm});
            skLineSegment(sketch, "E308", {"start": v(69, 69) * mm, "end": v(69, 64) * mm});
            skLineSegment(sketch, "E309", {"start": v(69, 64) * mm, "end": v(71, 64) * mm});
            skLineSegment(sketch, "E310", {"start": v(71, 64) * mm, "end": v(71, 69) * mm});
            skLineSegment(sketch, "E311", {"start": v(71, 69) * mm, "end": v(76, 69) * mm});
            skLineSegment(sketch, "E312", {"start": v(76, 69) * mm, "end": v(76, 71) * mm});
            skLineSegment(sketch, "E313", {"start": v(76, 71) * mm, "end": v(71, 71) * mm});
            skLineSegment(sketch, "E314", {"start": v(71, 71) * mm, "end": v(71, 76) * mm});
            skLineSegment(sketch, "E315", {"start": v(71, 76) * mm, "end": v(69, 76) * mm});
            skLineSegment(sketch, "E316", {"start": v(49, 76) * mm, "end": v(49, 71) * mm});
            skLineSegment(sketch, "E317", {"start": v(49, 71) * mm, "end": v(44, 71) * mm});
            skLineSegment(sketch, "E318", {"start": v(44, 71) * mm, "end": v(44, 69) * mm});
            skLineSegment(sketch, "E319", {"start": v(44, 69) * mm, "end": v(49, 69) * mm});
            skLineSegment(sketch, "E320", {"start": v(49, 69) * mm, "end": v(49, 64) * mm});
            skLineSegment(sketch, "E321", {"start": v(49, 64) * mm, "end": v(51, 64) * mm});
            skLineSegment(sketch, "E322", {"start": v(51, 64) * mm, "end": v(51, 69) * mm});
            skLineSegment(sketch, "E323", {"start": v(51, 69) * mm, "end": v(56, 69) * mm});
            skLineSegment(sketch, "E324", {"start": v(56, 69) * mm, "end": v(56, 71) * mm});
            skLineSegment(sketch, "E325", {"start": v(56, 71) * mm, "end": v(51, 71) * mm});
            skLineSegment(sketch, "E326", {"start": v(51, 71) * mm, "end": v(51, 76) * mm});
            skLineSegment(sketch, "E327", {"start": v(51, 76) * mm, "end": v(49, 76) * mm});
            skLineSegment(sketch, "E328", {"start": v(9, 116) * mm, "end": v(9, 111) * mm});
            skLineSegment(sketch, "E329", {"start": v(9, 111) * mm, "end": v(4, 111) * mm});
            skLineSegment(sketch, "E330", {"start": v(4, 111) * mm, "end": v(4, 109) * mm});
            skLineSegment(sketch, "E331", {"start": v(4, 109) * mm, "end": v(9, 109) * mm});
            skLineSegment(sketch, "E332", {"start": v(9, 109) * mm, "end": v(9, 104) * mm});
            skLineSegment(sketch, "E333", {"start": v(9, 104) * mm, "end": v(11, 104) * mm});
            skLineSegment(sketch, "E334", {"start": v(11, 104) * mm, "end": v(11, 109) * mm});
            skLineSegment(sketch, "E335", {"start": v(11, 109) * mm, "end": v(16, 109) * mm});
            skLineSegment(sketch, "E336", {"start": v(16, 109) * mm, "end": v(16, 111) * mm});
            skLineSegment(sketch, "E337", {"start": v(16, 111) * mm, "end": v(11, 111) * mm});
            skLineSegment(sketch, "E338", {"start": v(11, 111) * mm, "end": v(11, 116) * mm});
            skLineSegment(sketch, "E339", {"start": v(11, 116) * mm, "end": v(9, 116) * mm});
            skLineSegment(sketch, "E340", {"start": v(29, 116) * mm, "end": v(29, 111) * mm});
            skLineSegment(sketch, "E341", {"start": v(29, 111) * mm, "end": v(24, 111) * mm});
            skLineSegment(sketch, "E342", {"start": v(24, 111) * mm, "end": v(24, 109) * mm});
            skLineSegment(sketch, "E343", {"start": v(24, 109) * mm, "end": v(29, 109) * mm});
            skLineSegment(sketch, "E344", {"start": v(29, 109) * mm, "end": v(29, 104) * mm});
            skLineSegment(sketch, "E345", {"start": v(29, 104) * mm, "end": v(31, 104) * mm});
            skLineSegment(sketch, "E346", {"start": v(31, 104) * mm, "end": v(31, 109) * mm});
            skLineSegment(sketch, "E347", {"start": v(31, 109) * mm, "end": v(36, 109) * mm});
            skLineSegment(sketch, "E348", {"start": v(36, 109) * mm, "end": v(36, 111) * mm});
            skLineSegment(sketch, "E349", {"start": v(36, 111) * mm, "end": v(31, 111) * mm});
            skLineSegment(sketch, "E350", {"start": v(31, 111) * mm, "end": v(31, 116) * mm});
            skLineSegment(sketch, "E351", {"start": v(31, 116) * mm, "end": v(29, 116) * mm});
            skLineSegment(sketch, "E352", {"start": v(69, 116) * mm, "end": v(69, 111) * mm});
            skLineSegment(sketch, "E353", {"start": v(69, 111) * mm, "end": v(64, 111) * mm});
            skLineSegment(sketch, "E354", {"start": v(64, 111) * mm, "end": v(64, 109) * mm});
            skLineSegment(sketch, "E355", {"start": v(64, 109) * mm, "end": v(69, 109) * mm});
            skLineSegment(sketch, "E356", {"start": v(69, 109) * mm, "end": v(69, 104) * mm});
            skLineSegment(sketch, "E357", {"start": v(69, 104) * mm, "end": v(71, 104) * mm});
            skLineSegment(sketch, "E358", {"start": v(71, 104) * mm, "end": v(71, 109) * mm});
            skLineSegment(sketch, "E359", {"start": v(71, 109) * mm, "end": v(76, 109) * mm});
            skLineSegment(sketch, "E360", {"start": v(76, 109) * mm, "end": v(76, 111) * mm});
            skLineSegment(sketch, "E361", {"start": v(76, 111) * mm, "end": v(71, 111) * mm});
            skLineSegment(sketch, "E362", {"start": v(71, 111) * mm, "end": v(71, 116) * mm});
            skLineSegment(sketch, "E363", {"start": v(71, 116) * mm, "end": v(69, 116) * mm});
            skLineSegment(sketch, "E364", {"start": v(49, 116) * mm, "end": v(49, 111) * mm});
            skLineSegment(sketch, "E365", {"start": v(49, 111) * mm, "end": v(44, 111) * mm});
            skLineSegment(sketch, "E366", {"start": v(44, 111) * mm, "end": v(44, 109) * mm});
            skLineSegment(sketch, "E367", {"start": v(44, 109) * mm, "end": v(49, 109) * mm});
            skLineSegment(sketch, "E368", {"start": v(49, 109) * mm, "end": v(49, 104) * mm});
            skLineSegment(sketch, "E369", {"start": v(49, 104) * mm, "end": v(51, 104) * mm});
            skLineSegment(sketch, "E370", {"start": v(51, 104) * mm, "end": v(51, 109) * mm});
            skLineSegment(sketch, "E371", {"start": v(51, 109) * mm, "end": v(56, 109) * mm});
            skLineSegment(sketch, "E372", {"start": v(56, 109) * mm, "end": v(56, 111) * mm});
            skLineSegment(sketch, "E373", {"start": v(56, 111) * mm, "end": v(51, 111) * mm});
            skLineSegment(sketch, "E374", {"start": v(51, 111) * mm, "end": v(51, 116) * mm});
            skLineSegment(sketch, "E375", {"start": v(51, 116) * mm, "end": v(49, 116) * mm});
            skLineSegment(sketch, "E376.bottom", {"start": v(4, 51) * mm, "end": v(16, 51) * mm});
            skLineSegment(sketch, "E376.top", {"start": v(4, 49) * mm, "end": v(16, 49) * mm});
            skLineSegment(sketch, "E376.left", {"start": v(4, 51) * mm, "end": v(4, 49) * mm});
            skLineSegment(sketch, "E376.right", {"start": v(16, 51) * mm, "end": v(16, 49) * mm});
            skLineSegment(sketch, "E377.bottom", {"start": v(24, 51) * mm, "end": v(36, 51) * mm});
            skLineSegment(sketch, "E377.top", {"start": v(24, 49) * mm, "end": v(36, 49) * mm});
            skLineSegment(sketch, "E377.left", {"start": v(24, 51) * mm, "end": v(24, 49) * mm});
            skLineSegment(sketch, "E377.right", {"start": v(36, 51) * mm, "end": v(36, 49) * mm});
            skLineSegment(sketch, "E378.bottom", {"start": v(44, 51) * mm, "end": v(56, 51) * mm});
            skLineSegment(sketch, "E378.top", {"start": v(44, 49) * mm, "end": v(56, 49) * mm});
            skLineSegment(sketch, "E378.left", {"start": v(44, 51) * mm, "end": v(44, 49) * mm});
            skLineSegment(sketch, "E378.right", {"start": v(56, 51) * mm, "end": v(56, 49) * mm});
            skLineSegment(sketch, "E379.bottom", {"start": v(64, 51) * mm, "end": v(76, 51) * mm});
            skLineSegment(sketch, "E379.top", {"start": v(64, 49) * mm, "end": v(76, 49) * mm});
            skLineSegment(sketch, "E379.left", {"start": v(64, 51) * mm, "end": v(64, 49) * mm});
            skLineSegment(sketch, "E379.right", {"start": v(76, 51) * mm, "end": v(76, 49) * mm});
            skLineSegment(sketch, "E380.bottom", {"start": v(4, 91) * mm, "end": v(16, 91) * mm});
            skLineSegment(sketch, "E380.top", {"start": v(4, 89) * mm, "end": v(16, 89) * mm});
            skLineSegment(sketch, "E380.left", {"start": v(4, 91) * mm, "end": v(4, 89) * mm});
            skLineSegment(sketch, "E380.right", {"start": v(16, 91) * mm, "end": v(16, 89) * mm});
            skLineSegment(sketch, "E381.bottom", {"start": v(24, 91) * mm, "end": v(36, 91) * mm});
            skLineSegment(sketch, "E381.top", {"start": v(24, 89) * mm, "end": v(36, 89) * mm});
            skLineSegment(sketch, "E381.left", {"start": v(24, 91) * mm, "end": v(24, 89) * mm});
            skLineSegment(sketch, "E381.right", {"start": v(36, 91) * mm, "end": v(36, 89) * mm});
            skLineSegment(sketch, "E382.bottom", {"start": v(44, 91) * mm, "end": v(56, 91) * mm});
            skLineSegment(sketch, "E382.top", {"start": v(44, 89) * mm, "end": v(56, 89) * mm});
            skLineSegment(sketch, "E382.left", {"start": v(44, 91) * mm, "end": v(44, 89) * mm});
            skLineSegment(sketch, "E382.right", {"start": v(56, 91) * mm, "end": v(56, 89) * mm});
            skLineSegment(sketch, "E383.bottom", {"start": v(64, 91) * mm, "end": v(76, 91) * mm});
            skLineSegment(sketch, "E383.top", {"start": v(64, 89) * mm, "end": v(76, 89) * mm});
            skLineSegment(sketch, "E383.left", {"start": v(64, 91) * mm, "end": v(64, 89) * mm});
            skLineSegment(sketch, "E383.right", {"start": v(76, 91) * mm, "end": v(76, 89) * mm});
            skLineSegment(sketch, "E384.bottom", {"start": v(4, 131) * mm, "end": v(16, 131) * mm});
            skLineSegment(sketch, "E384.top", {"start": v(4, 129) * mm, "end": v(16, 129) * mm});
            skLineSegment(sketch, "E384.left", {"start": v(4, 131) * mm, "end": v(4, 129) * mm});
            skLineSegment(sketch, "E384.right", {"start": v(16, 131) * mm, "end": v(16, 129) * mm});
            skLineSegment(sketch, "E385.bottom", {"start": v(24, 131) * mm, "end": v(36, 131) * mm});
            skLineSegment(sketch, "E385.top", {"start": v(24, 129) * mm, "end": v(36, 129) * mm});
            skLineSegment(sketch, "E385.left", {"start": v(24, 131) * mm, "end": v(24, 129) * mm});
            skLineSegment(sketch, "E385.right", {"start": v(36, 131) * mm, "end": v(36, 129) * mm});
            skLineSegment(sketch, "E386.bottom", {"start": v(44, 131) * mm, "end": v(56, 131) * mm});
            skLineSegment(sketch, "E386.top", {"start": v(44, 129) * mm, "end": v(56, 129) * mm});
            skLineSegment(sketch, "E386.left", {"start": v(44, 131) * mm, "end": v(44, 129) * mm});
            skLineSegment(sketch, "E386.right", {"start": v(56, 131) * mm, "end": v(56, 129) * mm});
            skLineSegment(sketch, "E387.bottom", {"start": v(64, 131) * mm, "end": v(76, 131) * mm});
            skLineSegment(sketch, "E387.top", {"start": v(64, 129) * mm, "end": v(76, 129) * mm});
            skLineSegment(sketch, "E387.left", {"start": v(64, 131) * mm, "end": v(64, 129) * mm});
            skLineSegment(sketch, "E387.right", {"start": v(76, 131) * mm, "end": v(76, 129) * mm});
            skLineSegment(sketch, "E388.bottom", {"start": v(4, 11) * mm, "end": v(16, 11) * mm});
            skLineSegment(sketch, "E388.top", {"start": v(4, 9) * mm, "end": v(16, 9) * mm});
            skLineSegment(sketch, "E388.left", {"start": v(4, 11) * mm, "end": v(4, 9) * mm});
            skLineSegment(sketch, "E388.right", {"start": v(16, 11) * mm, "end": v(16, 9) * mm});
            skLineSegment(sketch, "E389.bottom", {"start": v(24, 11) * mm, "end": v(36, 11) * mm});
            skLineSegment(sketch, "E389.top", {"start": v(24, 9) * mm, "end": v(36, 9) * mm});
            skLineSegment(sketch, "E389.left", {"start": v(24, 11) * mm, "end": v(24, 9) * mm});
            skLineSegment(sketch, "E389.right", {"start": v(36, 11) * mm, "end": v(36, 9) * mm});
            skLineSegment(sketch, "E390.bottom", {"start": v(44, 11) * mm, "end": v(56, 11) * mm});
            skLineSegment(sketch, "E390.top", {"start": v(44, 9) * mm, "end": v(56, 9) * mm});
            skLineSegment(sketch, "E390.left", {"start": v(44, 11) * mm, "end": v(44, 9) * mm});
            skLineSegment(sketch, "E390.right", {"start": v(56, 11) * mm, "end": v(56, 9) * mm});
            skLineSegment(sketch, "E391.bottom", {"start": v(64, 11) * mm, "end": v(76, 11) * mm});
            skLineSegment(sketch, "E391.top", {"start": v(64, 9) * mm, "end": v(76, 9) * mm});
            skLineSegment(sketch, "E391.left", {"start": v(64, 11) * mm, "end": v(64, 9) * mm});
            skLineSegment(sketch, "E391.right", {"start": v(76, 11) * mm, "end": v(76, 9) * mm});
            skSolve(sketch);
        }
        {
            var Q0;
            Q0 = qSketchRegion(id + "F4", true);
            extrude(context, id + "F5", {"entities" : qUnion([Q0]), "operationType" : NewBodyOperationType.REMOVE, "oppositeDirection" : true, "depth" : 2 * mm, "offsetDistance" : 25 * mm});
        }
    });
